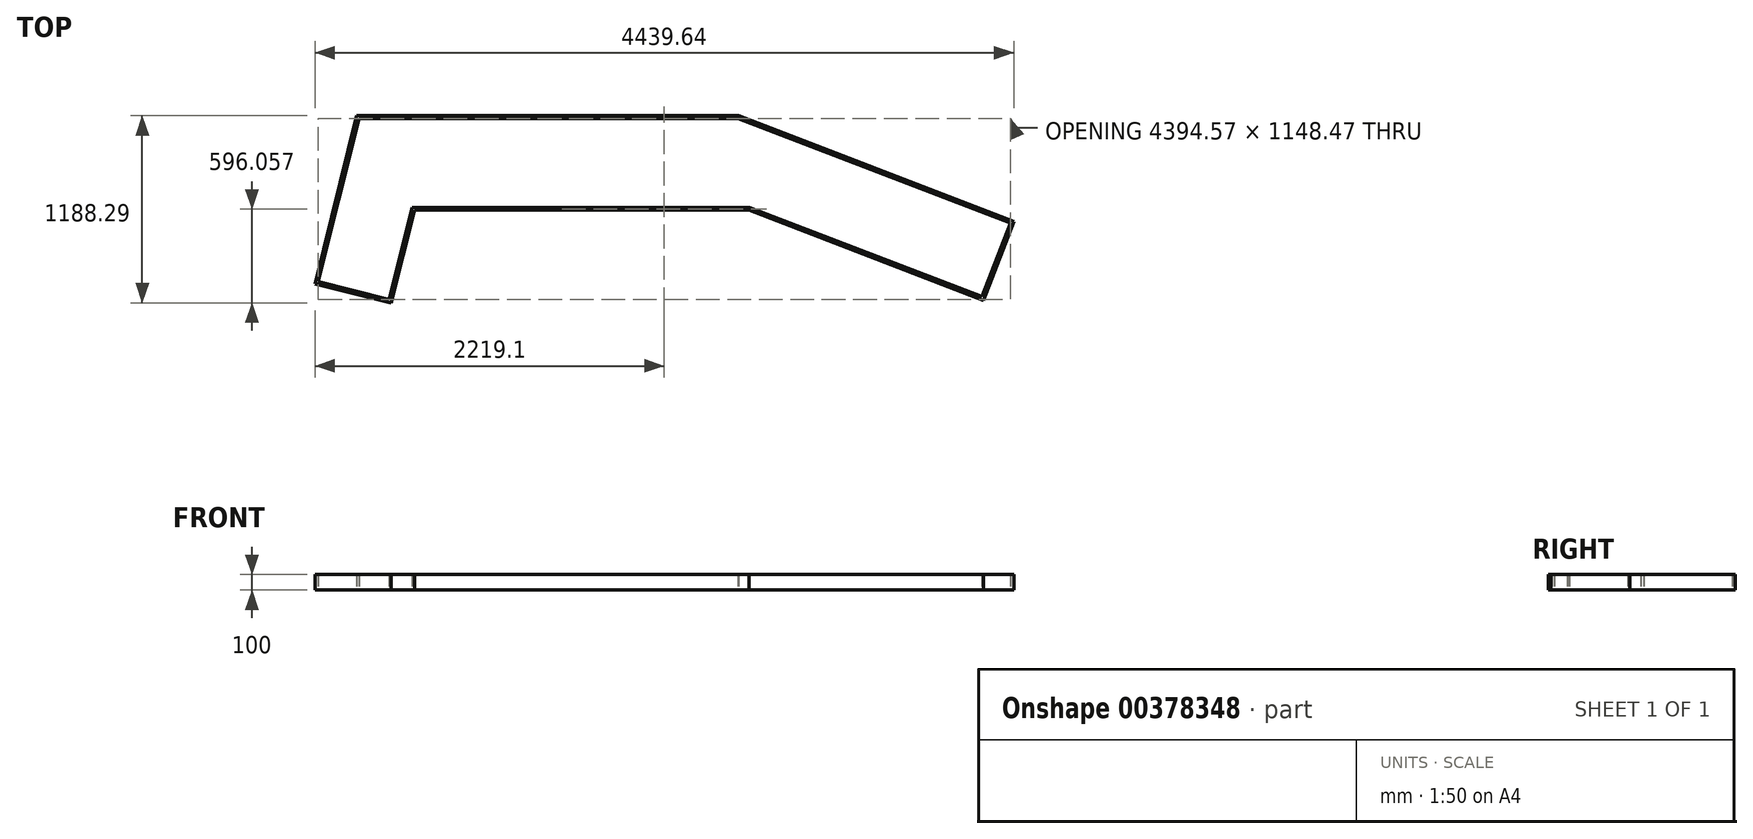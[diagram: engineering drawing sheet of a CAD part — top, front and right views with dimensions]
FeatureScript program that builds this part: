
annotation { "Feature Type Name" : "Feature", "Feature Type Description" : "" }
export const myFeature = defineFeature(function(context is Context, id is Id, definition is map)
    precondition{}
    {
        {
            var Q0;
            Q0=qCreatedBy(makeId("Top.planeOp"),FACE);
            var sketch = newSketch(context, id + "F0", { "sketchPlane" : qUnion([Q0])});
            skLineSegment(sketch, "E0.bottom", {"start": v(1291.38, -300) * mm, "end": v(-834.29, -300) * mm});
            skLineSegment(sketch, "E0.top", {"start": v(1224, 300) * mm, "end": v(-1200, 300) * mm});
            skPoint(sketch, "E0.middle", {"position": v(0, 0) * mm});
            skLineSegment(sketch, "E1", {"start": v(-1200, 300) * mm, "end": v(-1466.11, -767.33) * mm});
            skLineSegment(sketch, "E2", {"start": v(-1466.11, -767.33) * mm, "end": v(-980.97, -888.29) * mm});
            skLineSegment(sketch, "E3", {"start": v(-980.97, -888.29) * mm, "end": v(-834.29, -300) * mm});
            skLineSegment(sketch, "E4", {"start": v(1224, 300) * mm, "end": v(2973.53, -371.58) * mm});
            skLineSegment(sketch, "E5", {"start": v(2973.53, -371.58) * mm, "end": v(2781.44, -871.98) * mm});
            skLineSegment(sketch, "E6", {"start": v(2781.44, -871.98) * mm, "end": v(1291.38, -300) * mm});
            skPoint(sketch, "E7.orphan", {"position": v(-1224, -300) * mm});
            skPoint(sketch, "E8.orphan", {"position": v(1200, -300) * mm});
            skLineSegment(sketch, "E9.0", {"start": v(1220.66, 282) * mm, "end": v(-1185.94, 282) * mm});
            skLineSegment(sketch, "E9.1", {"start": v(1220.66, 282) * mm, "end": v(2950.27, -381.94) * mm});
            skLineSegment(sketch, "E9.2", {"start": v(-1185.94, 282) * mm, "end": v(-1444.3, -754.21) * mm});
            skLineSegment(sketch, "E9.3", {"start": v(2950.27, -381.94) * mm, "end": v(2771.1, -848.73) * mm});
            skLineSegment(sketch, "E9.4", {"start": v(-1444.3, -754.21) * mm, "end": v(-994.08, -866.47) * mm});
            skLineSegment(sketch, "E9.5", {"start": v(-994.08, -866.47) * mm, "end": v(-848.35, -282) * mm});
            skLineSegment(sketch, "E9.6", {"start": v(1294.72, -282) * mm, "end": v(-848.35, -282) * mm});
            skLineSegment(sketch, "E9.7", {"start": v(2771.1, -848.73) * mm, "end": v(1294.72, -282) * mm});
            skSolve(sketch);
        }
        {
            var Q0;
            Q0=makeQuery(id+"F0.imprint","IMPRINT",FACE,{"disambiguationData":[TD([[makeQuery(id+"F0.imprint","IMPRINT",EDGE,{"derivedFrom":sQuery(id+"F0.wireOp",EDGE,"E0.bottom")}),-1.0]])]});
            extrude(context, id + "F1", {"entities" : qUnion([Q0]), "depth" : 100 * mm});
        }
    });
